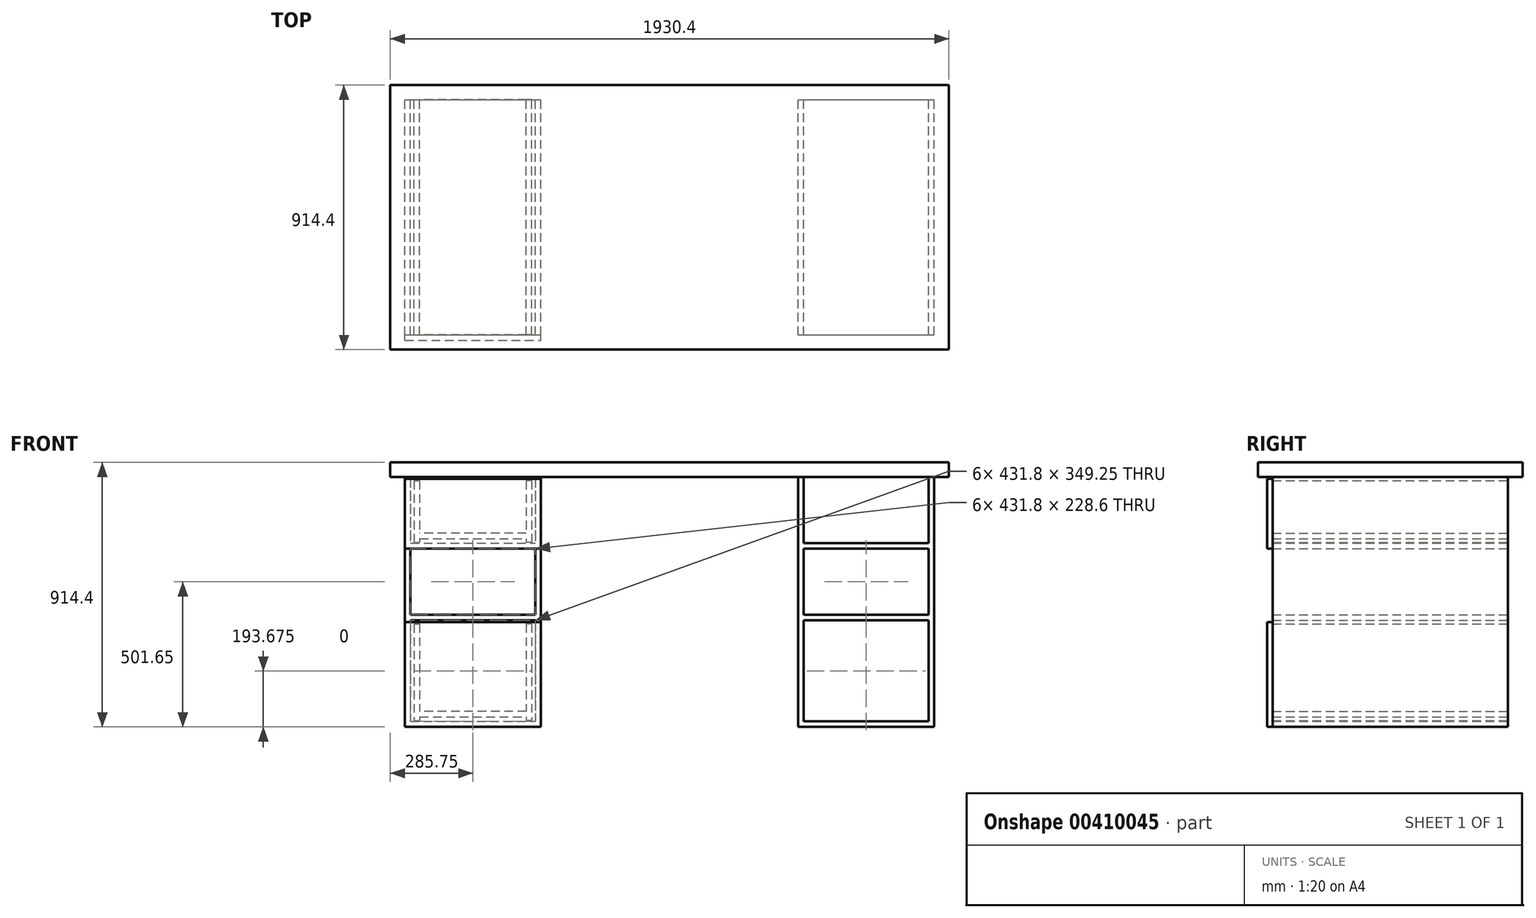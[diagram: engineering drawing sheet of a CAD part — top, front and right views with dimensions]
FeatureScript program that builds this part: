
annotation { "Feature Type Name" : "Feature", "Feature Type Description" : "" }
export const myFeature = defineFeature(function(context is Context, id is Id, definition is map)
    precondition{}
    {
        {
            var Q0;
            Q0=qCreatedBy(makeId("Front.planeOp"),FACE);
            var sketch = newSketch(context, id + "F0", { "sketchPlane" : qUnion([Q0])});
            skLineSegment(sketch, "E0.left", {"start": v(-914.4, 0) * mm, "end": v(-914.4, -844.55) * mm});
            skLineSegment(sketch, "E0.right", {"start": v(-895.35, 0) * mm, "end": v(-895.35, -844.55) * mm});
            skLineSegment(sketch, "E1.left", {"start": v(914.4, -844.55) * mm, "end": v(914.4, 0) * mm});
            skLineSegment(sketch, "E1.right", {"start": v(895.35, -844.55) * mm, "end": v(895.35, 0) * mm});
            skLineSegment(sketch, "E2.bottom", {"start": v(-965.2, 0) * mm, "end": v(965.2, 0) * mm});
            skLineSegment(sketch, "E2.top", {"start": v(-965.2, 50.8) * mm, "end": v(965.2, 50.8) * mm});
            skLineSegment(sketch, "E2.left", {"start": v(-965.2, 0) * mm, "end": v(-965.2, 50.8) * mm});
            skLineSegment(sketch, "E2.right", {"start": v(965.2, 0) * mm, "end": v(965.2, 50.8) * mm});
            skLineSegment(sketch, "E3.left", {"start": v(463.55, 0) * mm, "end": v(463.55, -844.55) * mm});
            skLineSegment(sketch, "E3.right", {"start": v(444.5, 0) * mm, "end": v(444.5, -844.55) * mm});
            skLineSegment(sketch, "E4.left", {"start": v(-463.55, 0) * mm, "end": v(-463.55, -844.55) * mm});
            skLineSegment(sketch, "E4.right", {"start": v(-444.5, 0) * mm, "end": v(-444.5, -844.55) * mm});
            skLineSegment(sketch, "E5.bottom", {"start": v(-914.4, -844.55) * mm, "end": v(-444.5, -844.55) * mm});
            skLineSegment(sketch, "E5.top", {"start": v(-914.4, -863.6) * mm, "end": v(-444.5, -863.6) * mm});
            skLineSegment(sketch, "E5.left", {"start": v(-914.4, -844.55) * mm, "end": v(-914.4, -863.6) * mm});
            skLineSegment(sketch, "E5.right", {"start": v(-444.5, -844.55) * mm, "end": v(-444.5, -863.6) * mm});
            skLineSegment(sketch, "E6.bottom", {"start": v(444.5, -844.55) * mm, "end": v(914.4, -844.55) * mm});
            skLineSegment(sketch, "E6.top", {"start": v(444.5, -863.6) * mm, "end": v(914.4, -863.6) * mm});
            skLineSegment(sketch, "E6.left", {"start": v(444.5, -844.55) * mm, "end": v(444.5, -863.6) * mm});
            skLineSegment(sketch, "E6.right", {"start": v(914.4, -844.55) * mm, "end": v(914.4, -863.6) * mm});
            skLineSegment(sketch, "E7", {"start": v(-895.35, -228.6) * mm, "end": v(-463.55, -228.6) * mm});
            skLineSegment(sketch, "E8", {"start": v(-895.35, -247.65) * mm, "end": v(-463.55, -247.65) * mm});
            skLineSegment(sketch, "E9", {"start": v(-895.35, -476.25) * mm, "end": v(-463.55, -476.25) * mm});
            skLineSegment(sketch, "E10", {"start": v(-463.55, -495.3) * mm, "end": v(-895.35, -495.3) * mm});
            skLineSegment(sketch, "E11", {"start": v(463.55, -247.65) * mm, "end": v(895.35, -247.65) * mm});
            skLineSegment(sketch, "E12", {"start": v(463.55, -228.6) * mm, "end": v(895.35, -228.6) * mm});
            skLineSegment(sketch, "E13", {"start": v(463.55, -476.25) * mm, "end": v(895.35, -476.25) * mm});
            skLineSegment(sketch, "E14", {"start": v(463.55, -495.3) * mm, "end": v(895.35, -495.3) * mm});
            skLineSegment(sketch, "E15.bottom", {"start": v(-882.65, -508) * mm, "end": v(-863.6, -508) * mm});
            skLineSegment(sketch, "E15.top", {"start": v(-882.65, -841.37) * mm, "end": v(-863.6, -841.37) * mm});
            skLineSegment(sketch, "E15.left", {"start": v(-882.65, -508) * mm, "end": v(-882.65, -841.37) * mm});
            skLineSegment(sketch, "E15.right", {"start": v(-863.6, -508) * mm, "end": v(-863.6, -841.37) * mm});
            skLineSegment(sketch, "E16", {"start": v(-863.6, -828.67) * mm, "end": v(-679.45, -828.67) * mm});
            skLineSegment(sketch, "E17", {"start": v(-863.6, -809.62) * mm, "end": v(-679.45, -809.62) * mm});
            skLineSegment(sketch, "E18", {"start": v(-882.65, -508) * mm, "end": v(-895.35, -495.3) * mm, "construction": true});
            skLineSegment(sketch, "E19", {"start": v(-679.45, -844.55) * mm, "end": v(-679.45, -739.13) * mm, "construction": true});
            skLineSegment(sketch, "E20.MirrorCS", {"start": v(-495.3, -809.62) * mm, "end": v(-679.45, -809.62) * mm});
            skLineSegment(sketch, "E21.MirrorCS", {"start": v(-495.3, -828.67) * mm, "end": v(-679.45, -828.67) * mm});
            skLineSegment(sketch, "E22.MirrorCS", {"start": v(-495.3, -508) * mm, "end": v(-495.3, -841.37) * mm});
            skLineSegment(sketch, "E23.MirrorCS", {"start": v(-476.25, -508) * mm, "end": v(-476.25, -841.37) * mm});
            skLineSegment(sketch, "E24.MirrorCS", {"start": v(-476.25, -841.37) * mm, "end": v(-495.3, -841.37) * mm});
            skLineSegment(sketch, "E25.MirrorCS", {"start": v(-476.25, -508) * mm, "end": v(-495.3, -508) * mm});
            skLineSegment(sketch, "E26.bottom", {"start": v(-882.65, -12.7) * mm, "end": v(-863.6, -12.7) * mm});
            skLineSegment(sketch, "E26.top", {"start": v(-882.65, -225.43) * mm, "end": v(-863.6, -225.43) * mm});
            skLineSegment(sketch, "E26.left", {"start": v(-882.65, -12.7) * mm, "end": v(-882.65, -225.43) * mm});
            skLineSegment(sketch, "E26.right", {"start": v(-863.6, -12.7) * mm, "end": v(-863.6, -225.43) * mm});
            skLineSegment(sketch, "E27", {"start": v(-863.6, -212.73) * mm, "end": v(-679.45, -212.73) * mm});
            skLineSegment(sketch, "E28", {"start": v(-895.35, 0) * mm, "end": v(-882.65, -12.7) * mm, "construction": true});
            skLineSegment(sketch, "E29", {"start": v(-863.6, -193.68) * mm, "end": v(-679.45, -193.68) * mm});
            skLineSegment(sketch, "E30.MirrorCS", {"start": v(-495.3, -193.68) * mm, "end": v(-679.45, -193.68) * mm});
            skLineSegment(sketch, "E31.MirrorCS", {"start": v(-495.3, -212.73) * mm, "end": v(-679.45, -212.73) * mm});
            skLineSegment(sketch, "E32.MirrorCS", {"start": v(-495.3, -12.7) * mm, "end": v(-495.3, -225.43) * mm});
            skLineSegment(sketch, "E33.MirrorCS", {"start": v(-476.25, -12.7) * mm, "end": v(-476.25, -225.43) * mm});
            skLineSegment(sketch, "E34.MirrorCS", {"start": v(-476.25, -12.7) * mm, "end": v(-495.3, -12.7) * mm});
            skLineSegment(sketch, "E35.MirrorCS", {"start": v(-476.25, -225.43) * mm, "end": v(-495.3, -225.43) * mm});
            skSolve(sketch);
        }
        {
            var Q0;
            {var subQ4=sQuery(id+"F0.wireOp",EDGE,"E0.left");Q0=makeQuery(id+"F0.imprint","IMPRINT",FACE,{"disambiguationData":[TD([[makeQuery(id+"F0.imprint","IMPRINT",EDGE,{"derivedFrom":subQ4}),1.0]])]});}
            var Q1;
            {var subQ5=sQuery(id+"F0.wireOp",EDGE,"E1.left");Q1=makeQuery(id+"F0.imprint","IMPRINT",FACE,{"disambiguationData":[TD([[makeQuery(id+"F0.imprint","IMPRINT",EDGE,{"derivedFrom":subQ5}),1.0]])]});}
            var Q2;
            {var subQ0=sQuery(id+"F0.wireOp",EDGE,"E11");Q2=makeQuery(id+"F0.imprint","IMPRINT",FACE,{"disambiguationData":[TD([[makeQuery(id+"F0.imprint","IMPRINT",EDGE,{"derivedFrom":subQ0}),1.0]])]});}
            var Q3;
            {var subQ0=sQuery(id+"F0.wireOp",EDGE,"E13");Q3=makeQuery(id+"F0.imprint","IMPRINT",FACE,{"disambiguationData":[TD([[makeQuery(id+"F0.imprint","IMPRINT",EDGE,{"derivedFrom":subQ0}),-1.0]])]});}
            var Q4;
            {var subQ6=sQuery(id+"F0.wireOp",EDGE,"E3.right");Q4=makeQuery(id+"F0.imprint","IMPRINT",FACE,{"disambiguationData":[TD([[makeQuery(id+"F0.imprint","IMPRINT",EDGE,{"derivedFrom":subQ6}),1.0]])]});}
            var Q5;
            Q5=makeQuery(id+"F0.imprint","IMPRINT",FACE,{"disambiguationData":[TD([[makeQuery(id+"F0.imprint","IMPRINT",EDGE,{"derivedFrom":sQuery(id+"F0.wireOp",EDGE,"E6.top")}),1.0]])]});
            var Q6;
            {var subQ0=sQuery(id+"F0.wireOp",EDGE,"E7");Q6=makeQuery(id+"F0.imprint","IMPRINT",FACE,{"disambiguationData":[TD([[makeQuery(id+"F0.imprint","IMPRINT",EDGE,{"derivedFrom":subQ0}),-1.0]])]});}
            var Q7;
            {var subQ0=sQuery(id+"F0.wireOp",EDGE,"E9");Q7=makeQuery(id+"F0.imprint","IMPRINT",FACE,{"disambiguationData":[TD([[makeQuery(id+"F0.imprint","IMPRINT",EDGE,{"derivedFrom":subQ0}),-1.0]])]});}
            var Q8;
            Q8=makeQuery(id+"F0.imprint","IMPRINT",FACE,{"disambiguationData":[TD([[makeQuery(id+"F0.imprint","IMPRINT",EDGE,{"derivedFrom":sQuery(id+"F0.wireOp",EDGE,"E5.top")}),1.0]])]});
            var Q9;
            {var subQ6=sQuery(id+"F0.wireOp",EDGE,"E4.right");Q9=makeQuery(id+"F0.imprint","IMPRINT",FACE,{"disambiguationData":[TD([[makeQuery(id+"F0.imprint","IMPRINT",EDGE,{"derivedFrom":subQ6}),-1.0]])]});}
            extrude(context, id + "F1", {"entities" : qUnion([Q0, Q1, Q2, Q3, Q4, Q5, Q6, Q7, Q8, Q9]), "endBound" : BoundingType.SYMMETRIC, "depth" : 812.8 * mm});
        }
        {
            var Q0;
            Q0=makeQuery(id+"F0.imprint","IMPRINT",FACE,{"disambiguationData":[TD([[makeQuery(id+"F0.imprint","IMPRINT",EDGE,{"derivedFrom":sQuery(id+"F0.wireOp",EDGE,"E2.top")}),-1.0]])]});
            extrude(context, id + "F2", {"entities" : qUnion([Q0]), "endBound" : BoundingType.SYMMETRIC, "depth" : 914.4 * mm});
        }
        {
            var Q0;
            Q0=makeQuery(id+"F0.imprint","IMPRINT",FACE,{"disambiguationData":[TD([[makeQuery(id+"F0.imprint","IMPRINT",EDGE,{"derivedFrom":sQuery(id+"F0.wireOp",EDGE,"E23.MirrorCS")}),-1.0]])]});
            var Q1;
            {var subQ2=sQuery(id+"F0.wireOp",EDGE,"E16");Q1=makeQuery(id+"F0.imprint","IMPRINT",FACE,{"disambiguationData":[TD([[makeQuery(id+"F0.imprint","IMPRINT",EDGE,{"derivedFrom":subQ2}),1.0]])]});}
            var Q2;
            {var subQ1=sQuery(id+"F0.wireOp",EDGE,"E15.bottom");Q2=makeQuery(id+"F0.imprint","IMPRINT",FACE,{"disambiguationData":[TD([[makeQuery(id+"F0.imprint","IMPRINT",EDGE,{"derivedFrom":subQ1}),-1.0]])]});}
            extrude(context, id + "F3", {"entities" : qUnion([Q0, Q1, Q2]), "endBound" : BoundingType.SYMMETRIC, "depth" : 812.8 * mm});
        }
        {
            var Q0;
            Q0=makeQuery(id+"F0.imprint","IMPRINT",FACE,{"disambiguationData":[TD([[makeQuery(id+"F0.imprint","IMPRINT",EDGE,{"derivedFrom":sQuery(id+"F0.wireOp",EDGE,"E33.MirrorCS")}),-1.0]])]});
            var Q1;
            {var subQ2=sQuery(id+"F0.wireOp",EDGE,"E27");Q1=makeQuery(id+"F0.imprint","IMPRINT",FACE,{"disambiguationData":[TD([[makeQuery(id+"F0.imprint","IMPRINT",EDGE,{"derivedFrom":subQ2}),1.0]])]});}
            var Q2;
            {var subQ1=sQuery(id+"F0.wireOp",EDGE,"E26.bottom");Q2=makeQuery(id+"F0.imprint","IMPRINT",FACE,{"disambiguationData":[TD([[makeQuery(id+"F0.imprint","IMPRINT",EDGE,{"derivedFrom":subQ1}),-1.0]])]});}
            extrude(context, id + "F4", {"entities" : qUnion([Q0, Q1, Q2]), "endBound" : BoundingType.SYMMETRIC, "depth" : 812.8 * mm});
        }
        {
            var Q0;
            Q0=makeQuery(id+"F1.opExtrude","CAP_VERTEX",VERTEX,{"disambiguationData":[OSD([sQuery(id+"F0.wireOp",EDGE,"E5.top"),sQuery(id+"F0.wireOp",EDGE,"E5.right")])],"isStart":false});
            var Q1;
            Q1=makeQuery(id+"F1.opExtrude","CAP_VERTEX",VERTEX,{"disambiguationData":[OSD([sQuery(id+"F0.wireOp",EDGE,"E2.bottom"),sQuery(id+"F0.wireOp",EDGE,"E3.right")])],"isStart":false});
            var Q2;
            Q2=makeQuery(id+"F1.opExtrude","CAP_VERTEX",VERTEX,{"disambiguationData":[OSD([sQuery(id+"F0.wireOp",EDGE,"E6.top"),sQuery(id+"F0.wireOp",EDGE,"E6.left")])],"isStart":false});
            cPlane(context, id + "F5", {"entities" : qUnion([Q0, Q1, Q2]), "cplaneType" : CPlaneType.THREE_POINT, "offset" : 25.4 * mm, "width" : 152.4 * mm, "height" : 152.4 * mm});
        }
        {
            var Q0;
            Q0=qCreatedBy(id+"F5.planeOp",FACE);
            var sketch = newSketch(context, id + "F6", { "sketchPlane" : qUnion([Q0])});
            skLineSegment(sketch, "E36.bottom", {"start": v(-914.4, -6.35) * mm, "end": v(-444.5, -6.35) * mm});
            skLineSegment(sketch, "E36.top", {"start": v(-914.4, -247.65) * mm, "end": v(-444.5, -247.65) * mm});
            skLineSegment(sketch, "E36.left", {"start": v(-914.4, -6.35) * mm, "end": v(-914.4, -247.65) * mm});
            skLineSegment(sketch, "E36.right", {"start": v(-444.5, -6.35) * mm, "end": v(-444.5, -247.65) * mm});
            skPoint(sketch, "E37.0", {"position": v(-895.35, -247.65) * mm});
            skPoint(sketch, "E38.0", {"position": v(-914.4, 0) * mm});
            skPoint(sketch, "E39.0", {"position": v(-444.5, 0) * mm});
            skLineSegment(sketch, "E40.bottom", {"start": v(-914.4, -501.65) * mm, "end": v(-444.5, -501.65) * mm});
            skLineSegment(sketch, "E40.top", {"start": v(-914.4, -863.6) * mm, "end": v(-444.5, -863.6) * mm});
            skLineSegment(sketch, "E40.left", {"start": v(-914.4, -501.65) * mm, "end": v(-914.4, -863.6) * mm});
            skLineSegment(sketch, "E40.right", {"start": v(-444.5, -501.65) * mm, "end": v(-444.5, -863.6) * mm});
            skSolve(sketch);
        }
        {
            var Q0;
            Q0 = qSketchRegion(id + "F6", true);
            extrude(context, id + "F7", {"entities" : qUnion([Q0]), "depth" : 19.05 * mm});
        }
    });
